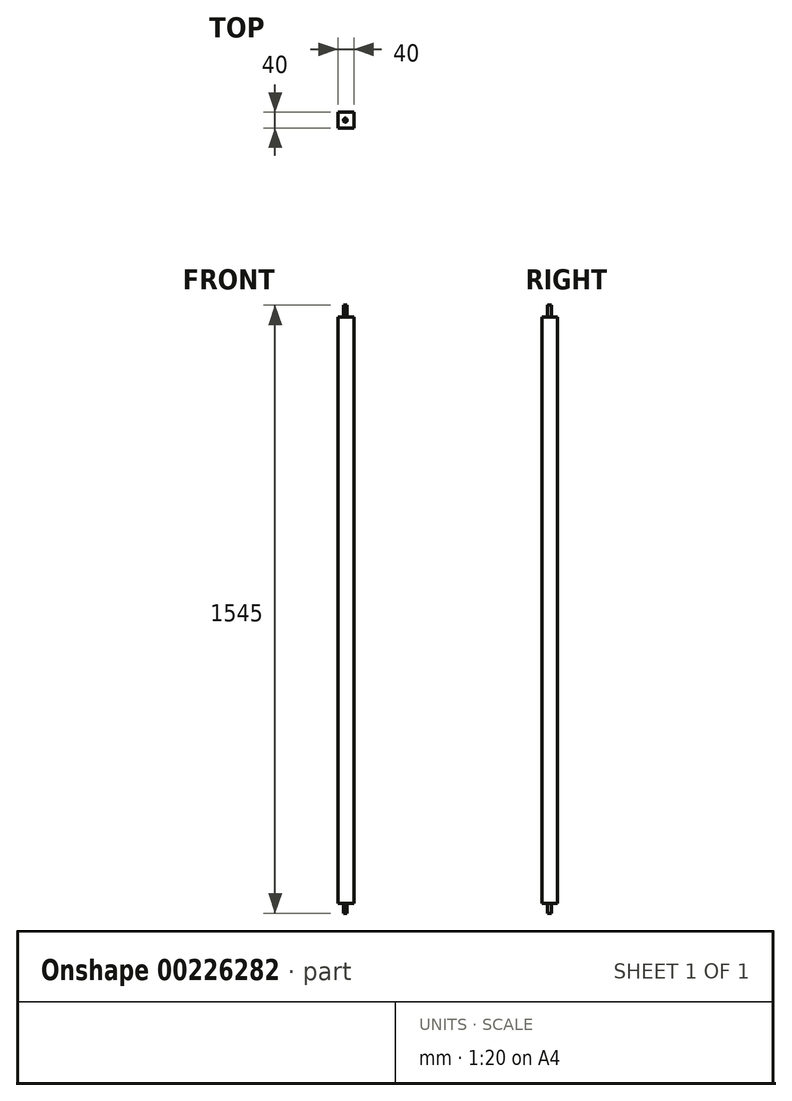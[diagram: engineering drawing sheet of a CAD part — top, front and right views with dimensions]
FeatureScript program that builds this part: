
annotation { "Feature Type Name" : "Feature", "Feature Type Description" : "" }
export const myFeature = defineFeature(function(context is Context, id is Id, definition is map)
    precondition{}
    {
        {
            var Q0;
            Q0=qCreatedBy(makeId("Top.planeOp"),FACE);
            var sketch = newSketch(context, id + "F0", { "sketchPlane" : qUnion([Q0])});
            skLineSegment(sketch, "E0.bottom", {"start": v(21.79, 20) * mm, "end": v(-18.21, 20) * mm});
            skLineSegment(sketch, "E0.top", {"start": v(21.79, -20) * mm, "end": v(-18.21, -20) * mm});
            skLineSegment(sketch, "E0.left", {"start": v(21.79, 20) * mm, "end": v(21.79, -20) * mm});
            skLineSegment(sketch, "E0.right", {"start": v(-18.21, 20) * mm, "end": v(-18.21, -20) * mm});
            skPoint(sketch, "E0.middle", {"position": v(1.79, 0) * mm});
            skSolve(sketch);
        }
        {
            var Q0;
            Q0 = qSketchRegion(id + "F0", true);
            var Q1;
            Q1=makeQuery(id+"F0.imprint","IMPRINT",FACE,{"disambiguationData":[TD([[makeQuery(id+"F0.imprint","IMPRINT",EDGE,{"derivedFrom":sQuery(id+"F0.wireOp",EDGE,"E0.bottom")}),1.0]])]});
            extrude(context, id + "F1", {"entities" : qUnion([Q0, Q1]), "depth" : 1490 * mm});
        }
        {
            var Q0;
            Q0=makeQuery(id+"F1.opExtrude","CAP_FACE",FACE,{"disambiguationData":[OSD([sQuery(id+"F0.wireOp",EDGE,"E0.bottom"),sQuery(id+"F0.wireOp",EDGE,"E0.top"),sQuery(id+"F0.wireOp",EDGE,"E0.left"),sQuery(id+"F0.wireOp",EDGE,"E0.right")])],"isStart":false});
            var sketch = newSketch(context, id + "F2", { "sketchPlane" : qUnion([Q0])});
            skCircle(sketch, "E1", {"center": v(0, 0) * mm, "radius": 4.9 * mm});
            skSolve(sketch);
        }
        {
            var Q0;
            Q0=makeQuery(id+"F2.imprint","IMPRINT",FACE,{"disambiguationData":[TD([[makeQuery(id+"F2.imprint","IMPRINT",EDGE,{"derivedFrom":sQuery(id+"F2.wireOp",EDGE,"E1")}),1.0]])]});
            extrude(context, id + "F3", {"entities" : qUnion([Q0]), "operationType" : NewBodyOperationType.ADD, "depth" : 30 * mm});
        }
        {
            var Q0;
            Q0=makeQuery(id+"F1.opExtrude","CAP_FACE",FACE,{"disambiguationData":[OSD([sQuery(id+"F0.wireOp",EDGE,"E0.bottom"),sQuery(id+"F0.wireOp",EDGE,"E0.top"),sQuery(id+"F0.wireOp",EDGE,"E0.left"),sQuery(id+"F0.wireOp",EDGE,"E0.right")])],"isStart":true});
            var sketch = newSketch(context, id + "F4", { "sketchPlane" : qUnion([Q0])});
            skCircle(sketch, "E2", {"center": v(0, 0) * mm, "radius": 4.9 * mm});
            skSolve(sketch);
        }
        {
            var Q0;
            Q0 = qSketchRegion(id + "F4", true);
            extrude(context, id + "F5", {"entities" : qUnion([Q0]), "operationType" : NewBodyOperationType.ADD, "depth" : 25 * mm});
        }
    });
